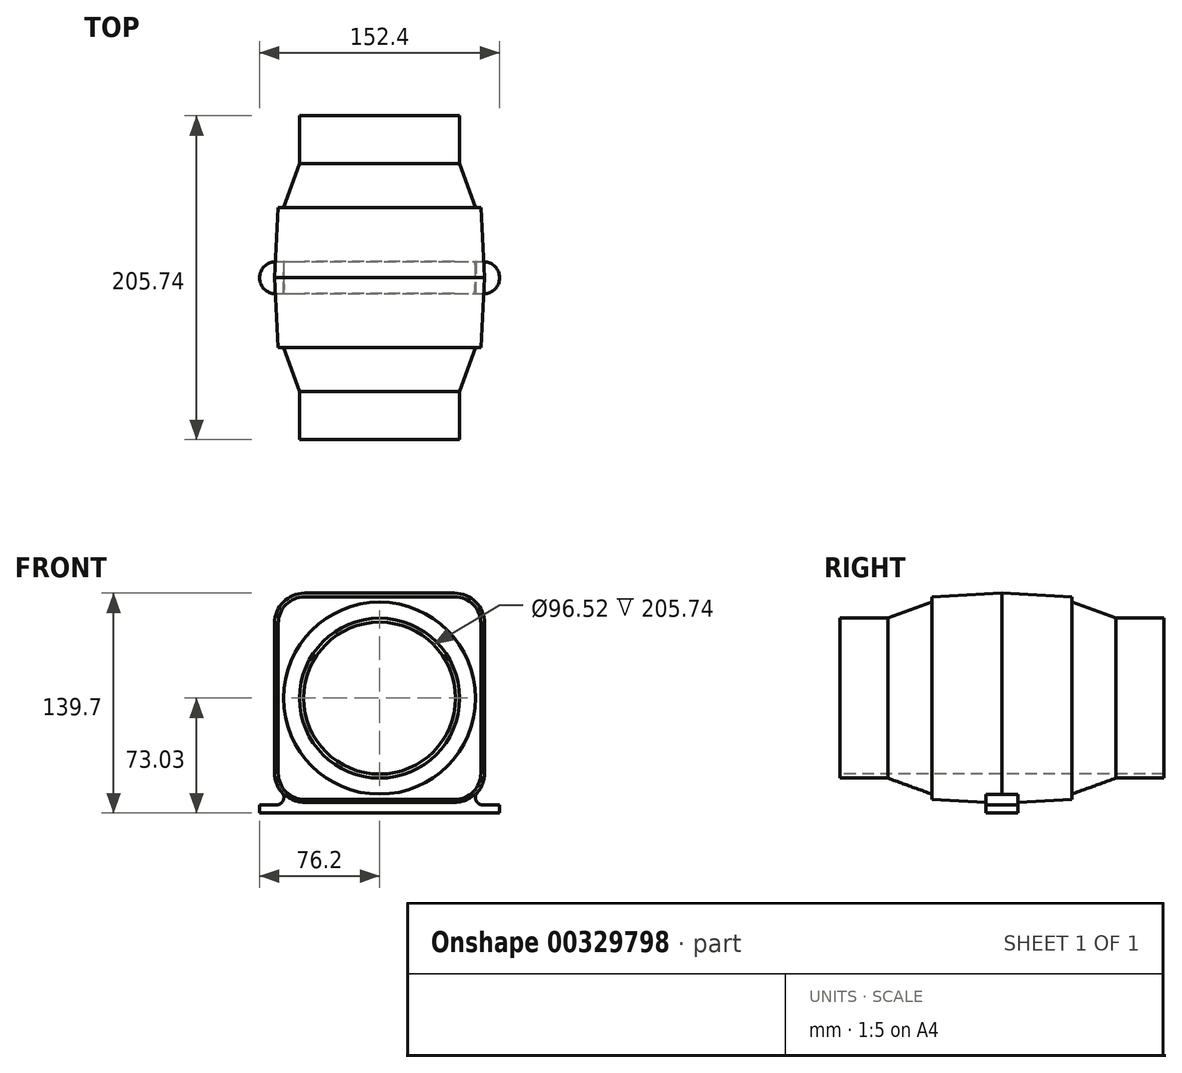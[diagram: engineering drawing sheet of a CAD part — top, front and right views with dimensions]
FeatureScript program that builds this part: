
annotation { "Feature Type Name" : "Feature", "Feature Type Description" : "" }
export const myFeature = defineFeature(function(context is Context, id is Id, definition is map)
    precondition{}
    {
        {
            var Q0;
            Q0=qCreatedBy(makeId("Front.planeOp"),FACE);
            var sketch = newSketch(context, id + "F0", { "sketchPlane" : qUnion([Q0])});
            skLineSegment(sketch, "E0.bottom", {"start": v(47.63, -66.68) * mm, "end": v(-47.63, -66.68) * mm});
            skLineSegment(sketch, "E0.top", {"start": v(47.63, 66.68) * mm, "end": v(-47.63, 66.68) * mm});
            skLineSegment(sketch, "E0.left", {"start": v(66.68, -47.62) * mm, "end": v(66.67, 47.63) * mm});
            skLineSegment(sketch, "E0.right", {"start": v(-66.67, -47.63) * mm, "end": v(-66.68, 47.62) * mm});
            skPoint(sketch, "E0.middle", {"position": v(0, 0) * mm});
            skPoint(sketch, "E1.visualSharp", {"position": v(66.67, 66.68) * mm});
            skArc(sketch, "E1.filletArc", {"start": v(66.68, 47.63) * mm, "mid": v(61.1, 61.1) * mm, "end": v(47.63, 66.68) * mm});
            skPoint(sketch, "E2.visualSharp", {"position": v(-66.68, 66.67) * mm});
            skArc(sketch, "E2.filletArc", {"start": v(-47.63, 66.68) * mm, "mid": v(-61.1, 61.1) * mm, "end": v(-66.68, 47.62) * mm});
            skPoint(sketch, "E3.visualSharp", {"position": v(-66.67, -66.68) * mm});
            skArc(sketch, "E3.filletArc", {"start": v(-66.68, -47.63) * mm, "mid": v(-61.1, -61.1) * mm, "end": v(-47.63, -66.68) * mm});
            skPoint(sketch, "E4.visualSharp", {"position": v(66.68, -66.67) * mm});
            skArc(sketch, "E4.filletArc", {"start": v(47.63, -66.67) * mm, "mid": v(61.1, -61.1) * mm, "end": v(66.68, -47.62) * mm});
            skSolve(sketch);
        }
        {
            var Q0;
            Q0 = qSketchRegion(id + "F0", true);
            extrude(context, id + "F1", {"entities" : qUnion([Q0]), "depth" : 44.45 * mm, "hasDraft" : true, "draftAngle" : 3 * degree, "draftPullDirection" : true, "hasSecondDirectionDraft" : true, "secondDirectionDraftAngle" : 3 * degree, "secondDirectionDraftPullDirection" : true});
        }
        {
            var Q0;
            Q0=makeQuery(id+"F1.opExtrude","CAP_FACE",FACE,{"disambiguationData":[OSD([sQuery(id+"F0.wireOp",EDGE,"E0.bottom"),sQuery(id+"F0.wireOp",EDGE,"E0.top"),sQuery(id+"F0.wireOp",EDGE,"E0.left"),sQuery(id+"F0.wireOp",EDGE,"E0.right"),sQuery(id+"F0.wireOp",EDGE,"E1.filletArc"),sQuery(id+"F0.wireOp",EDGE,"E2.filletArc"),sQuery(id+"F0.wireOp",EDGE,"E3.filletArc"),sQuery(id+"F0.wireOp",EDGE,"E4.filletArc")])],"isStart":false});
            var sketch = newSketch(context, id + "F2", { "sketchPlane" : qUnion([Q0])});
            skCircle(sketch, "E5", {"center": v(0, 0) * mm, "radius": 60.96 * mm});
            skSolve(sketch);
        }
        {
            var Q0;
            Q0 = qSketchRegion(id + "F2", true);
            extrude(context, id + "F3", {"entities" : qUnion([Q0]), "operationType" : NewBodyOperationType.ADD, "depth" : 27.94 * mm, "hasDraft" : true, "draftAngle" : 20 * degree, "draftPullDirection" : true});
        }
        {
            var Q0;
            Q0=makeQuery(id+"F3.opExtrude","CAP_FACE",FACE,{"disambiguationData":[OSD([sQuery(id+"F2.wireOp",EDGE,"E5")])],"isStart":false});
            var sketch = newSketch(context, id + "F4", { "sketchPlane" : qUnion([Q0])});
            skCircle(sketch, "E6", {"center": v(0, 0) * mm, "radius": 50.8 * mm});
            skSolve(sketch);
        }
        {
            var Q0;
            Q0 = qSketchRegion(id + "F4", true);
            extrude(context, id + "F5", {"entities" : qUnion([Q0]), "operationType" : NewBodyOperationType.ADD, "depth" : 30.48 * mm});
        }
        {
            var Q0;
            Q0=qCreatedBy(makeId("Front.planeOp"),FACE);
            var sketch = newSketch(context, id + "F6", { "sketchPlane" : qUnion([Q0])});
            skLineSegment(sketch, "E7.bottom", {"start": v(-76.2, -67.95) * mm, "end": v(-65.86, -67.95) * mm});
            skLineSegment(sketch, "E7.top", {"start": v(-76.2, -73.03) * mm, "end": v(76.2, -73.02) * mm});
            skLineSegment(sketch, "E7.left", {"start": v(-76.2, -67.95) * mm, "end": v(-76.2, -73.03) * mm});
            skLineSegment(sketch, "E7.right", {"start": v(76.2, -67.94) * mm, "end": v(76.2, -73.02) * mm});
            skArc(sketch, "E8", {"start": v(-65.86, -67.95) * mm, "mid": v(-61.69, -65.76) * mm, "end": v(-61.1, -61.1) * mm});
            skArc(sketch, "E9.MirrorCS", {"start": v(65.86, -67.95) * mm, "mid": v(61.69, -65.76) * mm, "end": v(61.1, -61.1) * mm});
            skPoint(sketch, "E10.orphan", {"position": v(-67.39, -67.7) * mm});
            skPoint(sketch, "E11.orphan", {"position": v(67.39, -67.7) * mm});
            skLineSegment(sketch, "E12.trimOffspring", {"start": v(65.86, -67.94) * mm, "end": v(76.2, -67.94) * mm});
            skLineSegment(sketch, "E13", {"start": v(-61.1, -61.1) * mm, "end": v(61.1, -61.1) * mm});
            skSolve(sketch);
        }
        {
            var Q0;
            Q0 = qSketchRegion(id + "F6", true);
            extrude(context, id + "F7", {"entities" : qUnion([Q0]), "operationType" : NewBodyOperationType.ADD, "depth" : 10.16 * mm});
        }
        {
            var Q0;
            Q0=makeQuery(id+"F7.opExtrude","CAP_EDGE",EDGE,{"disambiguationData":[OSD([sQuery(id+"F6.wireOp",EDGE,"E7.right")])],"isStart":false});
            var Q1;
            Q1=makeQuery(id+"F7.opExtrude","CAP_EDGE",EDGE,{"disambiguationData":[OSD([sQuery(id+"F6.wireOp",EDGE,"E7.left")])],"isStart":false});
            fillet(context, id + "F8", {"entities" : qUnion([Q0, Q1]), "radius" : 10.16 * mm, "tangentPropagation" : true, "allowEdgeOverflow" : false});
        }
        {
            var Q0;
            Q0=makeQuery(id+"F1.opExtrude","SWEPT_BODY",BODY,{"disambiguationData":[OSD([sQuery(id+"F0.wireOp",EDGE,"E0.bottom"),sQuery(id+"F0.wireOp",EDGE,"E0.top"),sQuery(id+"F0.wireOp",EDGE,"E0.left"),sQuery(id+"F0.wireOp",EDGE,"E0.right"),sQuery(id+"F0.wireOp",EDGE,"E1.filletArc"),sQuery(id+"F0.wireOp",EDGE,"E2.filletArc"),sQuery(id+"F0.wireOp",EDGE,"E3.filletArc"),sQuery(id+"F0.wireOp",EDGE,"E4.filletArc")])]});
            var Q1;
            Q1=qCreatedBy(makeId("Front.planeOp"),FACE);
            mirror(context, id + "F9", {"operationType" : NewBodyOperationType.ADD, "entities" : qUnion([Q0]), "mirrorPlane" : qUnion([Q1])});
        }
        {
            var Q0;
            Q0=makeQuery(id+"F5.opExtrude","CAP_FACE",FACE,{"disambiguationData":[OSD([sQuery(id+"F4.wireOp",EDGE,"E6")])],"isStart":false});
            var sketch = newSketch(context, id + "F10", { "sketchPlane" : qUnion([Q0])});
            skCircle(sketch, "E14", {"center": v(0, 0) * mm, "radius": 48.26 * mm});
            skSolve(sketch);
        }
        {
            var Q0;
            Q0 = qSketchRegion(id + "F10", true);
            extrude(context, id + "F11", {"entities" : qUnion([Q0]), "operationType" : NewBodyOperationType.REMOVE, "endBound" : BoundingType.THROUGH_ALL, "oppositeDirection" : true, "depth" : 25.4 * mm});
        }
    });
